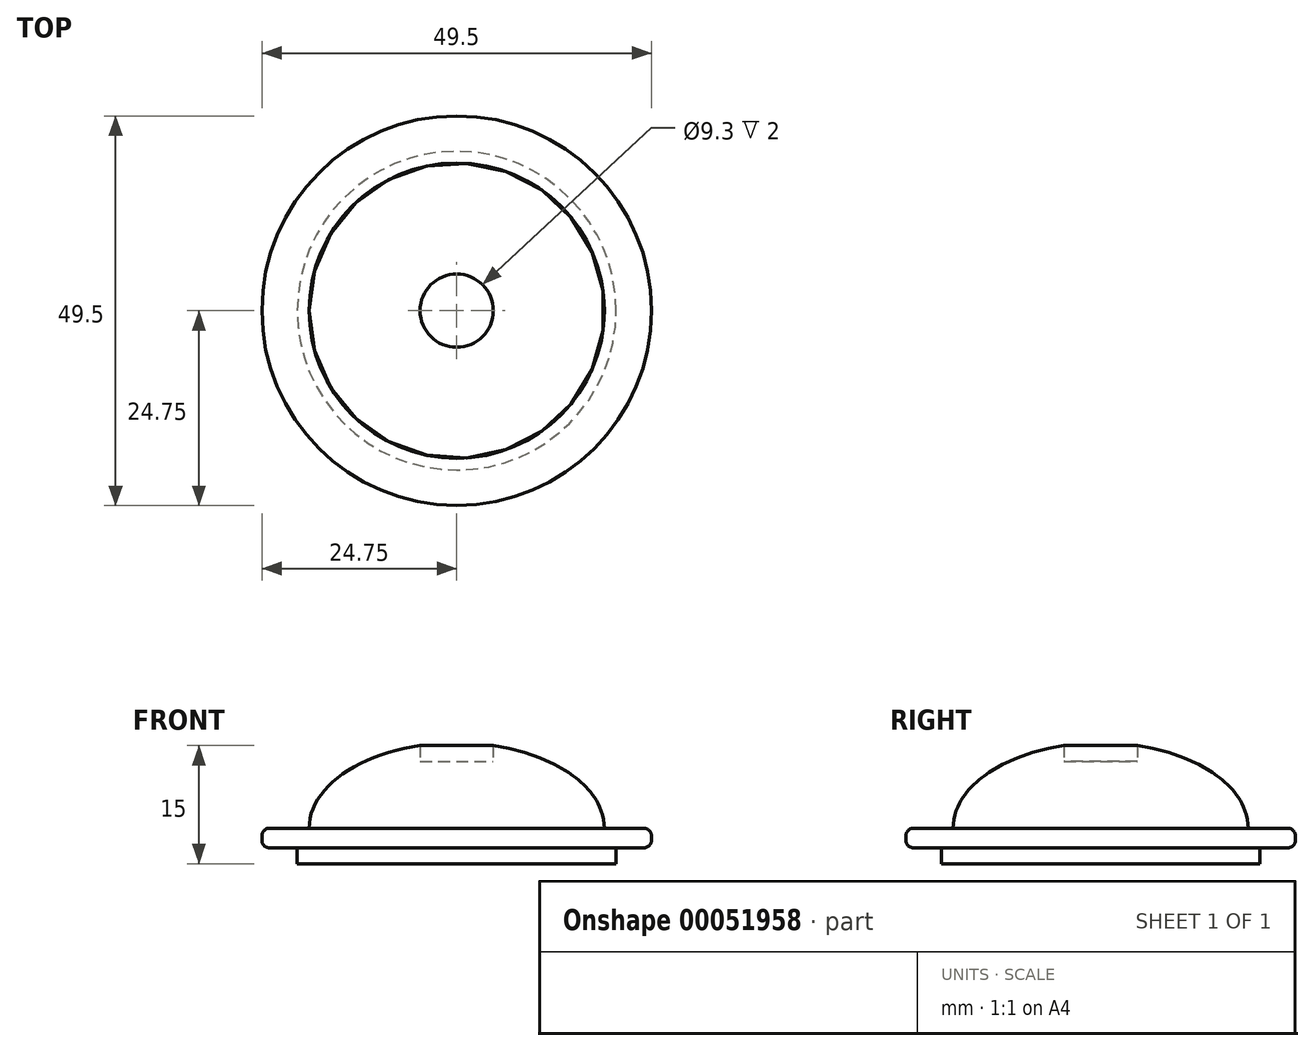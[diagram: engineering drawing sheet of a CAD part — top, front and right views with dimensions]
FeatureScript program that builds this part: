
annotation { "Feature Type Name" : "Feature", "Feature Type Description" : "" }
export const myFeature = defineFeature(function(context is Context, id is Id, definition is map)
    precondition{}
    {
        {
            var Q0;
            Q0=qCreatedBy(makeId("Front.planeOp"),FACE);
            var sketch = newSketch(context, id + "F0", { "sketchPlane" : qUnion([Q0])});
            skLineSegment(sketch, "E0", {"start": v(0, 0) * mm, "end": v(-20.25, 0) * mm});
            skLineSegment(sketch, "E1", {"start": v(-20.25, 0) * mm, "end": v(-20.25, 2) * mm});
            skLineSegment(sketch, "E2", {"start": v(-20.25, 2) * mm, "end": v(-24.75, 2) * mm});
            skLineSegment(sketch, "E3", {"start": v(-24.75, 2) * mm, "end": v(-24.75, 4.5) * mm});
            skLineSegment(sketch, "E4", {"start": v(-24.75, 4.5) * mm, "end": v(-18.75, 4.5) * mm});
            skLineSegment(sketch, "E5", {"start": v(0, 0) * mm, "end": v(0, 13) * mm});
            skEllipticalArc(sketch, "E6", {});
            skLineSegment(sketch, "E7", {"start": v(-4.65, 15) * mm, "end": v(-4.65, 13) * mm});
            skLineSegment(sketch, "E8", {"start": v(-4.65, 13) * mm, "end": v(0, 13) * mm});
            const initialGuessF0  = {"E6": [0, 0.0045, -1, 0, 0.01875, 0.010838597434793805, 4.963004193472405, 0]};
            skSetInitialGuess(sketch, initialGuessF0);
            skSolve(sketch);
        }
        {
            var Q0;
            Q0=makeQuery(id+"F0.imprint","IMPRINT",FACE,{"disambiguationData":[TD([[makeQuery(id+"F0.imprint","IMPRINT",EDGE,{"derivedFrom":sQuery(id+"F0.wireOp",EDGE,"E0")}),-1.0]])]});
            var Q1;
            Q1=sQuery(id+"F0.wireOp",EDGE,"E5");
            revolve(context, id + "F1", {"entities" : qUnion([Q0]), "axis" : qUnion([Q1]), "revolveType" : RevolveType.FULL});
        }
        {
            var Q0;
            Q0=makeQuery(id+"F1.opRevolve","SWEPT_EDGE",EDGE,{"disambiguationData":[OSD([sQuery(id+"F0.wireOp",EDGE,"E3"),sQuery(id+"F0.wireOp",EDGE,"E4")])]});
            var Q1;
            Q1=makeQuery(id+"F1.opRevolve","SWEPT_EDGE",EDGE,{"disambiguationData":[OSD([sQuery(id+"F0.wireOp",EDGE,"E2"),sQuery(id+"F0.wireOp",EDGE,"E3")])]});
            fillet(context, id + "F2", {"entities" : qUnion([Q0, Q1]), "radius" : 1 * mm, "tangentPropagation" : true, "allowEdgeOverflow" : false});
        }
    });
